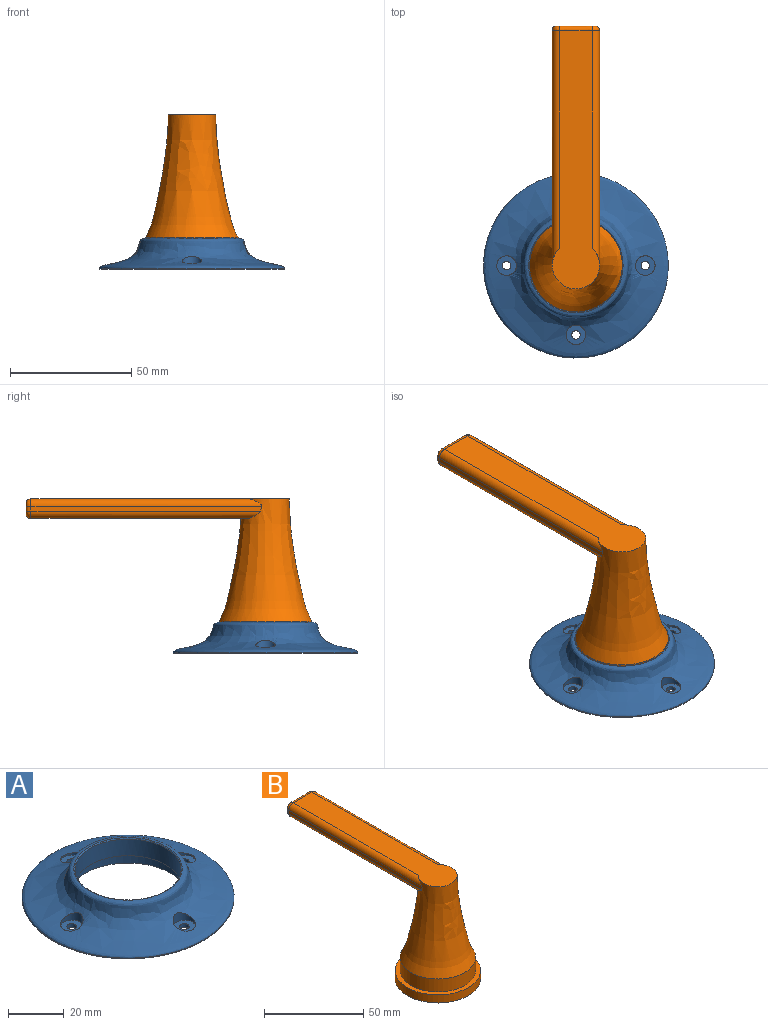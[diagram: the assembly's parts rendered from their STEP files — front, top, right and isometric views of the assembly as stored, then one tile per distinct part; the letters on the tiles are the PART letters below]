
ASSEMBLY  parts=2 mates=1
PART A: 19 faces, bbox 76.3x152.6x12.7 mm
  f0: plane 76.2x76.2mm, normal (0,0,-1), area 3057.5mm2, adj f1,f13,f14,f15,f16,f17
  f1: cylinder r=38.1mm len=76.2mm, axis (0,0,-1), area 69.9mm2, adj f0,f3
  f2: cylinder r=19.05mm len=38.1mm, axis (0,0,-1), area 874mm2, adj f4,f18
  f3: bspline ~152.58x76.29mm, area 4016.3mm2, adj f1,f4,f5,f7,f9,f11
  f4: torus R=19.44mm, axis (0,0,-1), area 76.3mm2, adj f2,f3
  f5: cylinder r=4.04mm len=8.08mm, axis (0,0,1), area 47.9mm2, adj f3,f6
  f6: plane 8.08x8.08mm, normal (0,0,1), area 41.7mm2, adj f5,f16
  f7: cylinder r=4.04mm len=8.08mm, axis (0,0,1), area 48mm2, adj f3,f8
  f8: plane 8.08x8.08mm, normal (0,0,1), area 41.7mm2, adj f7,f15
  f9: cylinder r=4.04mm len=8.08mm, axis (0,0,1), area 48mm2, adj f3,f10
  f10: plane 8.08x8.08mm, normal (0,0,1), area 41.7mm2, adj f9,f14
  f11: cylinder r=4.04mm len=8.08mm, axis (0,0,1), area 48mm2, adj f3,f12
  f12: plane 8.08x8.08mm, normal (0,0,1), area 41.7mm2, adj f11,f13
  f13: cylinder r=1.75mm len=3.5mm, axis (0,0,1), area 17.6mm2, adj f0,f12
  f14: cylinder r=1.75mm len=3.5mm, axis (0,0,1), area 17.6mm2, adj f0,f10
  f15: cylinder r=1.75mm len=3.5mm, axis (0,0,1), area 17.6mm2, adj f0,f8
  f16: cylinder r=1.75mm len=3.5mm, axis (0,0,1), area 17.6mm2, adj f0,f6
  f17: cylinder r=21.59mm len=43.18mm, axis (0,0,-1), area 678.3mm2, adj f0,f18
  f18: plane 43.18x43.18mm, normal (0,0,-1), area 324.3mm2, adj f2,f17
PART B: 31 faces, bbox 43.2x137.2x63.6 mm
  f0: cylinder r=21.59mm len=43.18mm, axis (0,0,-1), area 678.3mm2, adj f1,f2
  f1: plane 43.18x43.18mm, normal (0,0,1), area 324.3mm2, adj f0,f3
  f2: plane 43.18x43.18mm, normal (0,0,-1), area 1361.2mm2, adj f0,f22,f23,f24,f25
  f3: cylinder r=19.05mm len=38.1mm, axis (0,0,-1), area 961.1mm2, adj f1,f4
  f4: bspline ~77.08x50.81mm, area 3991.9mm2, adj f3,f5,f6,f7,f9,f10,f11,f12
  f5: plane 106.39x19.49mm, normal (0,0,1), area 1481.7mm2, adj f4,f10,f11,f18
  f6: plane 95.17x2.04mm, normal (1,0,0), area 189.8mm2, adj f4,f11,f13,f14
  f7: plane 95.17x2.04mm, normal (-1,0,0), area 189.8mm2, adj f4,f10,f12,f21
  f8: plane 15.49x4mm, normal (0,1,0), area 61.1mm2, adj f14,f15,f16,f17,f18,f19,f20,f21
  f9: plane 89.11x13.49mm, normal (0,0,-1), area 1177.9mm2, adj f4,f12,f13,f17
  f10: cylinder r=3mm len=95.13mm, axis (0,-1,0), area 435.3mm2, adj f4,f5,f7,f20
  f11: cylinder r=3mm len=95.13mm, axis (0,1,0), area 435.3mm2, adj f4,f5,f6,f16
  f12: cylinder r=3mm len=94.65mm, axis (0,1,0), area 433mm2, adj f4,f7,f9,f19
  f13: cylinder r=3mm len=94.65mm, axis (0,-1,0), area 433mm2, adj f4,f6,f9,f15
  f14: bspline ~2x2mm, area 6.5mm2, adj f6,f8,f15,f16
  f15: bspline ~3x3mm, area 11.8mm2, adj f8,f13,f14,f17
  f16: bspline ~3x3mm, area 11.8mm2, adj f8,f11,f14,f18
  f17: bspline ~13.49x2mm, area 43.9mm2, adj f8,f9,f15,f19
  f18: bspline ~13.49x2mm, area 43.9mm2, adj f5,f8,f16,f20
  f19: bspline ~3x3mm, area 11.8mm2, adj f8,f12,f17,f21
  f20: bspline ~3x3mm, area 11.8mm2, adj f8,f10,f18,f21
  f21: bspline ~2x2mm, area 6.5mm2, adj f7,f8,f19,f20
  f22: plane 38.1x10.16mm, normal (-1,0,0), area 378.8mm2, adj f2,f23,f25,f26,f30
  f23: plane 38.1x10.16mm, normal (0,-1,0), area 378.8mm2, adj f2,f22,f24,f26,f29
  f24: plane 38.1x10.16mm, normal (1,0,0), area 378.8mm2, adj f2,f23,f25,f26,f28
  f25: plane 38.1x10.16mm, normal (0,1,0), area 378.8mm2, adj f2,f22,f24,f26,f27
  f26: plane 10.16x10.16mm, normal (0,0,-1), area 103.2mm2, adj f22,f23,f24,f25
  f27: sphere r=5.33mm, area 8.5mm2, adj f25
  f28: sphere r=5.33mm, area 8.5mm2, adj f24
  f29: sphere r=5.33mm, area 8.5mm2, adj f23
  f30: sphere r=5.33mm, area 8.5mm2, adj f22
PLACE A t=(79.95,-10.37,10.53)mm
PLACE B t=(-0.05,-10.37,10.53)mm
MATE revolute A.f17 <-> B.f0  axis (0,0,-1) through (-0.05,-10.37,13.03)mm
